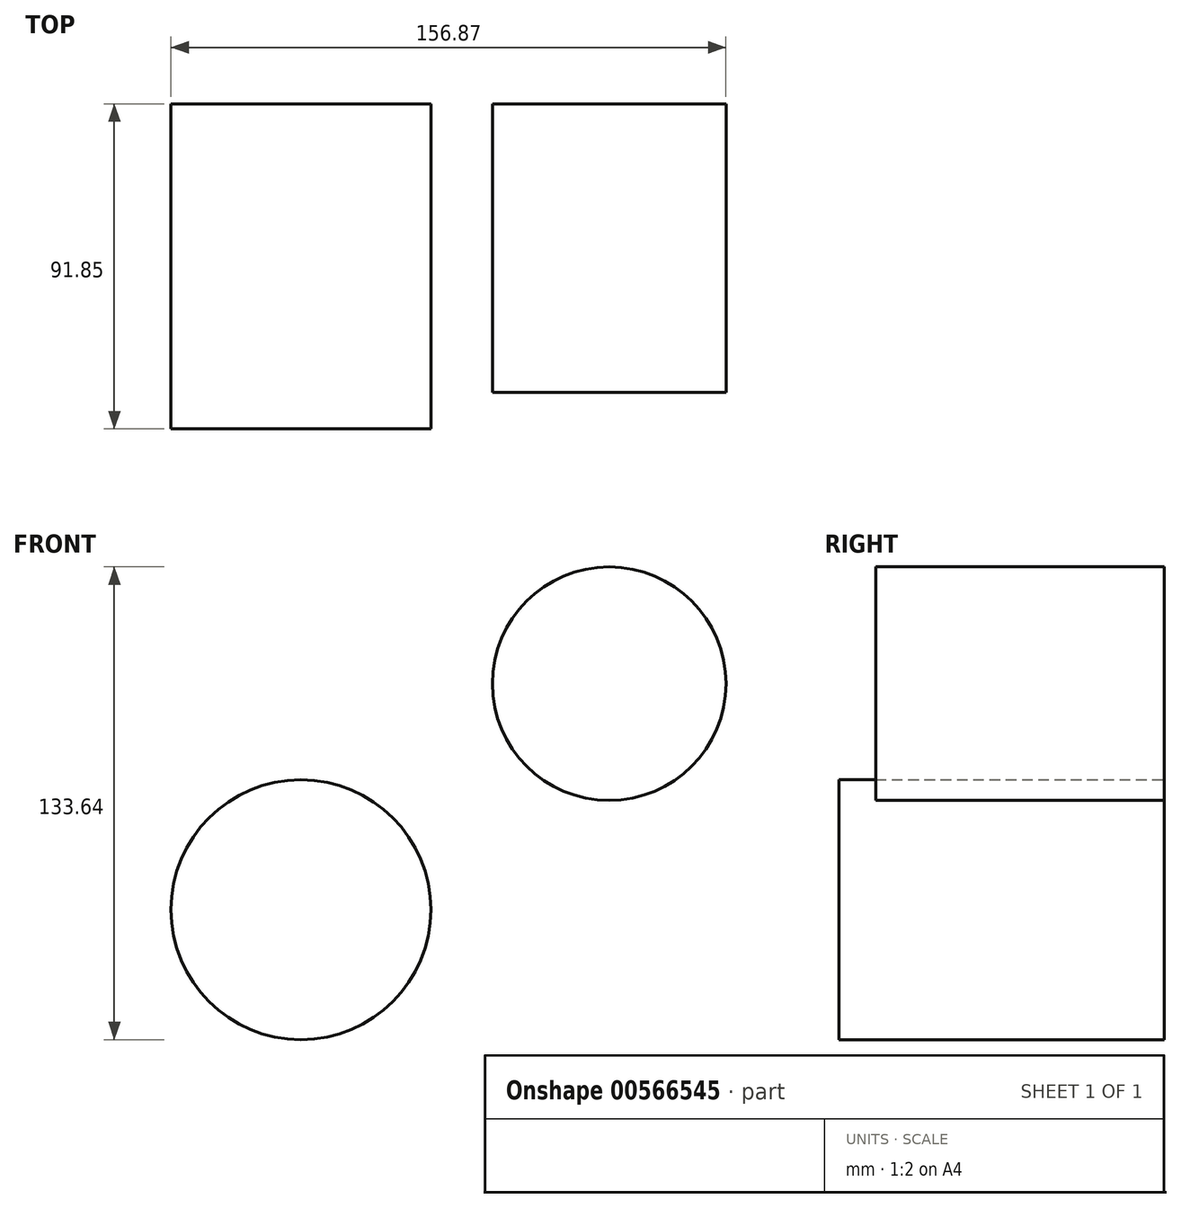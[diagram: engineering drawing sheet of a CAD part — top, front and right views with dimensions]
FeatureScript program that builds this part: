
annotation { "Feature Type Name" : "Feature", "Feature Type Description" : "" }
export const myFeature = defineFeature(function(context is Context, id is Id, definition is map)
    precondition{}
    {
        {
            var Q0;
            Q0=qCreatedBy(makeId("Front.planeOp"),FACE);
            var sketch = newSketch(context, id + "F0", { "sketchPlane" : qUnion([Q0])});
            skCircle(sketch, "E0", {"center": v(0, 0) * mm, "radius": 36.73 * mm});
            skCircle(sketch, "E1", {"center": v(87.13, 63.9) * mm, "radius": 33.01 * mm});
            skSolve(sketch);
        }
        {
            var Q0;
            Q0=makeQuery(id+"F0.imprint","IMPRINT",FACE,{"disambiguationData":[TD([[makeQuery(id+"F0.imprint","IMPRINT",EDGE,{"derivedFrom":sQuery(id+"F0.wireOp",EDGE,"E0")}),1.0]])]});
            var Q1;
            Q1=sQuery(id+"F0.wireOp",EDGE,"E0");
            extrude(context, id + "F1", {"entities" : qUnion([Q0]), "surfaceEntities" : qUnion([Q1]), "depth" : 91.85 * mm, "offsetDistance" : 25.4 * mm});
        }
        {
            var Q0;
            Q0=makeQuery(id+"F0.imprint","IMPRINT",FACE,{"disambiguationData":[TD([[makeQuery(id+"F0.imprint","IMPRINT",EDGE,{"derivedFrom":sQuery(id+"F0.wireOp",EDGE,"E1")}),1.0]])]});
            extrude(context, id + "F2", {"entities" : qUnion([Q0]), "depth" : 81.56 * mm, "offsetDistance" : 25.4 * mm});
        }
    });
